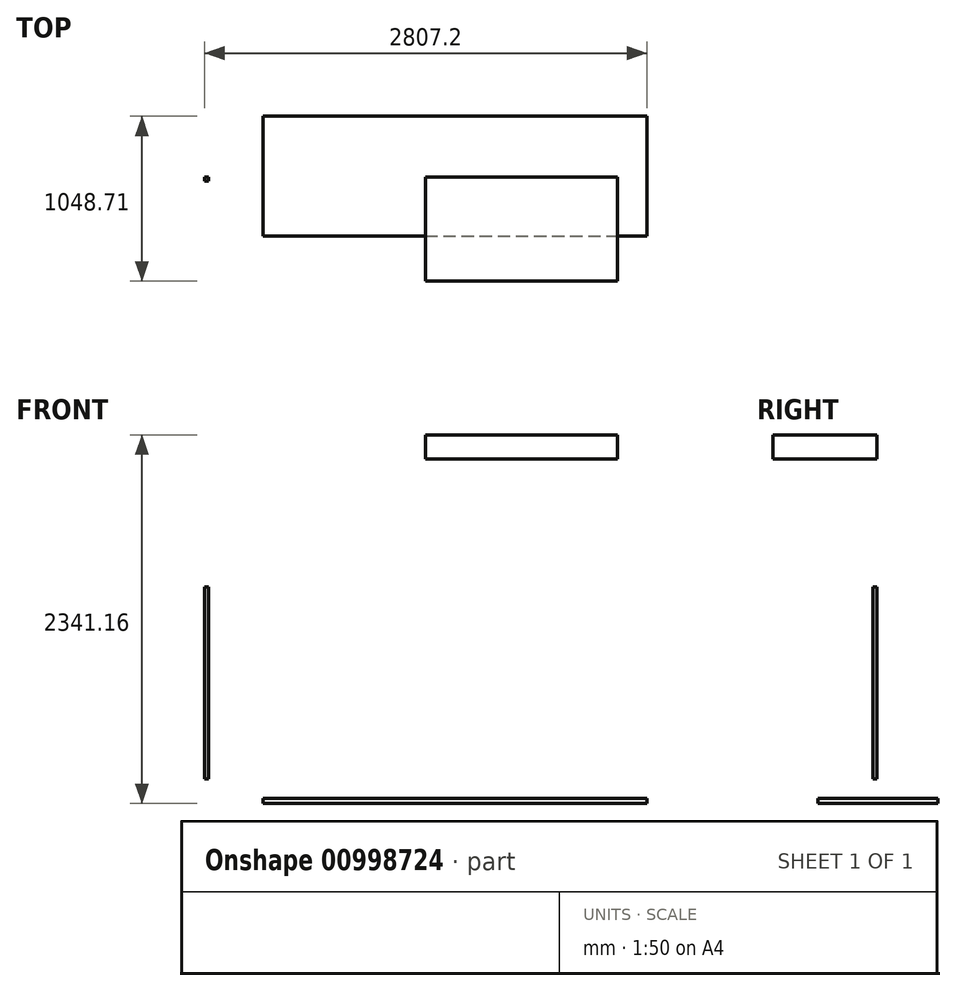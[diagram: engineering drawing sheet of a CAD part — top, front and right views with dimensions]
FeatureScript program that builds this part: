
annotation { "Feature Type Name" : "Feature", "Feature Type Description" : "" }
export const myFeature = defineFeature(function(context is Context, id is Id, definition is map)
    precondition{}
    {
        {
            var Q0;
            Q0=qCreatedBy(makeId("Top.planeOp"),FACE);
            var sketch = newSketch(context, id + "F0", { "sketchPlane" : qUnion([Q0])});
            skLineSegment(sketch, "E0.bottom", {"start": v(-1215.19, 388.3) * mm, "end": v(1223.21, 388.3) * mm});
            skLineSegment(sketch, "E0.top", {"start": v(-1215.19, -373.7) * mm, "end": v(1223.21, -373.7) * mm});
            skLineSegment(sketch, "E0.left", {"start": v(-1215.19, 388.3) * mm, "end": v(-1215.19, -373.7) * mm});
            skLineSegment(sketch, "E0.right", {"start": v(1223.21, 388.3) * mm, "end": v(1223.21, -373.7) * mm});
            skSolve(sketch);
        }
        {
            var Q0;
            Q0=makeQuery(id+"F0.imprint","IMPRINT",FACE,{"disambiguationData":[TD([[makeQuery(id+"F0.imprint","IMPRINT",EDGE,{"derivedFrom":sQuery(id+"F0.wireOp",EDGE,"E0.bottom")}),-1.0]])]});
            extrude(context, id + "F1", {"entities" : qUnion([Q0]), "depth" : 29.97 * mm, "offsetDistance" : 25.4 * mm});
        }
        {
            var Q0;
            Q0=qCreatedBy(makeId("Front.planeOp"),FACE);
            var sketch = newSketch(context, id + "F2", { "sketchPlane" : qUnion([Q0])});
            skLineSegment(sketch, "E1.bottom", {"start": v(-1769.16, 446.22) * mm, "end": v(-1615.4, 446.22) * mm});
            skLineSegment(sketch, "E1.top", {"start": v(-1769.16, 0) * mm, "end": v(-1615.4, 0) * mm});
            skLineSegment(sketch, "E1.left", {"start": v(-1769.16, 446.22) * mm, "end": v(-1769.16, 0) * mm});
            skLineSegment(sketch, "E1.right", {"start": v(-1615.4, 446.22) * mm, "end": v(-1615.4, 0) * mm});
            skSolve(sketch);
        }
        {
            var Q0;
            Q0=makeQuery(id+"F2.imprint","IMPRINT",FACE,{"disambiguationData":[TD([[makeQuery(id+"F2.imprint","IMPRINT",EDGE,{"derivedFrom":sQuery(id+"F2.wireOp",EDGE,"E1.bottom")}),-1.0]])]});
            extrude(context, id + "F3", {"entities" : qUnion([Q0]), "depth" : 25.4 * mm, "offsetDistance" : 25.4 * mm});
        }
        {
            var Q0;
            Q0=makeQuery(id+"F3.opExtrude","SWEPT_BODY",BODY,{"disambiguationData":[OSD([sQuery(id+"F2.wireOp",EDGE,"E1.bottom"),sQuery(id+"F2.wireOp",EDGE,"E1.top"),sQuery(id+"F2.wireOp",EDGE,"E1.left"),sQuery(id+"F2.wireOp",EDGE,"E1.right")])]});
            deleteBodies(context, id + "F4", {"entities" : qUnion([Q0])});
        }
        {
            var Q0;
            Q0=qCreatedBy(makeId("Front.planeOp"),FACE);
            var sketch = newSketch(context, id + "F5", { "sketchPlane" : qUnion([Q0])});
            skLineSegment(sketch, "E2.bottom", {"start": v(-1583.99, 1374.35) * mm, "end": v(-1558.59, 1374.35) * mm});
            skLineSegment(sketch, "E2.top", {"start": v(-1583.99, 155.15) * mm, "end": v(-1558.59, 155.15) * mm});
            skLineSegment(sketch, "E2.left", {"start": v(-1583.99, 1374.35) * mm, "end": v(-1583.99, 155.15) * mm});
            skLineSegment(sketch, "E2.right", {"start": v(-1558.59, 1374.35) * mm, "end": v(-1558.59, 155.15) * mm});
            skSolve(sketch);
        }
        {
            var Q0;
            Q0=makeQuery(id+"F5.imprint","IMPRINT",FACE,{"disambiguationData":[TD([[makeQuery(id+"F5.imprint","IMPRINT",EDGE,{"derivedFrom":sQuery(id+"F5.wireOp",EDGE,"E2.bottom")}),-1.0]])]});
            extrude(context, id + "F6", {"entities" : qUnion([Q0]), "depth" : 25.4 * mm, "offsetDistance" : 25.4 * mm});
        }
        {
            var Q0;
            Q0=qCreatedBy(makeId("Front.planeOp"),FACE);
            var sketch = newSketch(context, id + "F7", { "sketchPlane" : qUnion([Q0])});
            skLineSegment(sketch, "E3.bottom", {"start": v(-183.24, 2341.16) * mm, "end": v(1035.96, 2341.16) * mm});
            skLineSegment(sketch, "E3.top", {"start": v(-183.24, 2188.76) * mm, "end": v(1035.96, 2188.76) * mm});
            skLineSegment(sketch, "E3.left", {"start": v(-183.24, 2341.16) * mm, "end": v(-183.24, 2188.76) * mm});
            skLineSegment(sketch, "E3.right", {"start": v(1035.96, 2341.16) * mm, "end": v(1035.96, 2188.76) * mm});
            skSolve(sketch);
        }
        {
            var Q0;
            Q0=makeQuery(id+"F7.imprint","IMPRINT",FACE,{"disambiguationData":[TD([[makeQuery(id+"F7.imprint","IMPRINT",EDGE,{"derivedFrom":sQuery(id+"F7.wireOp",EDGE,"E3.bottom")}),-1.0]])]});
            extrude(context, id + "F8", {"entities" : qUnion([Q0]), "depth" : 660.4 * mm, "offsetDistance" : 25.4 * mm});
        }
    });
